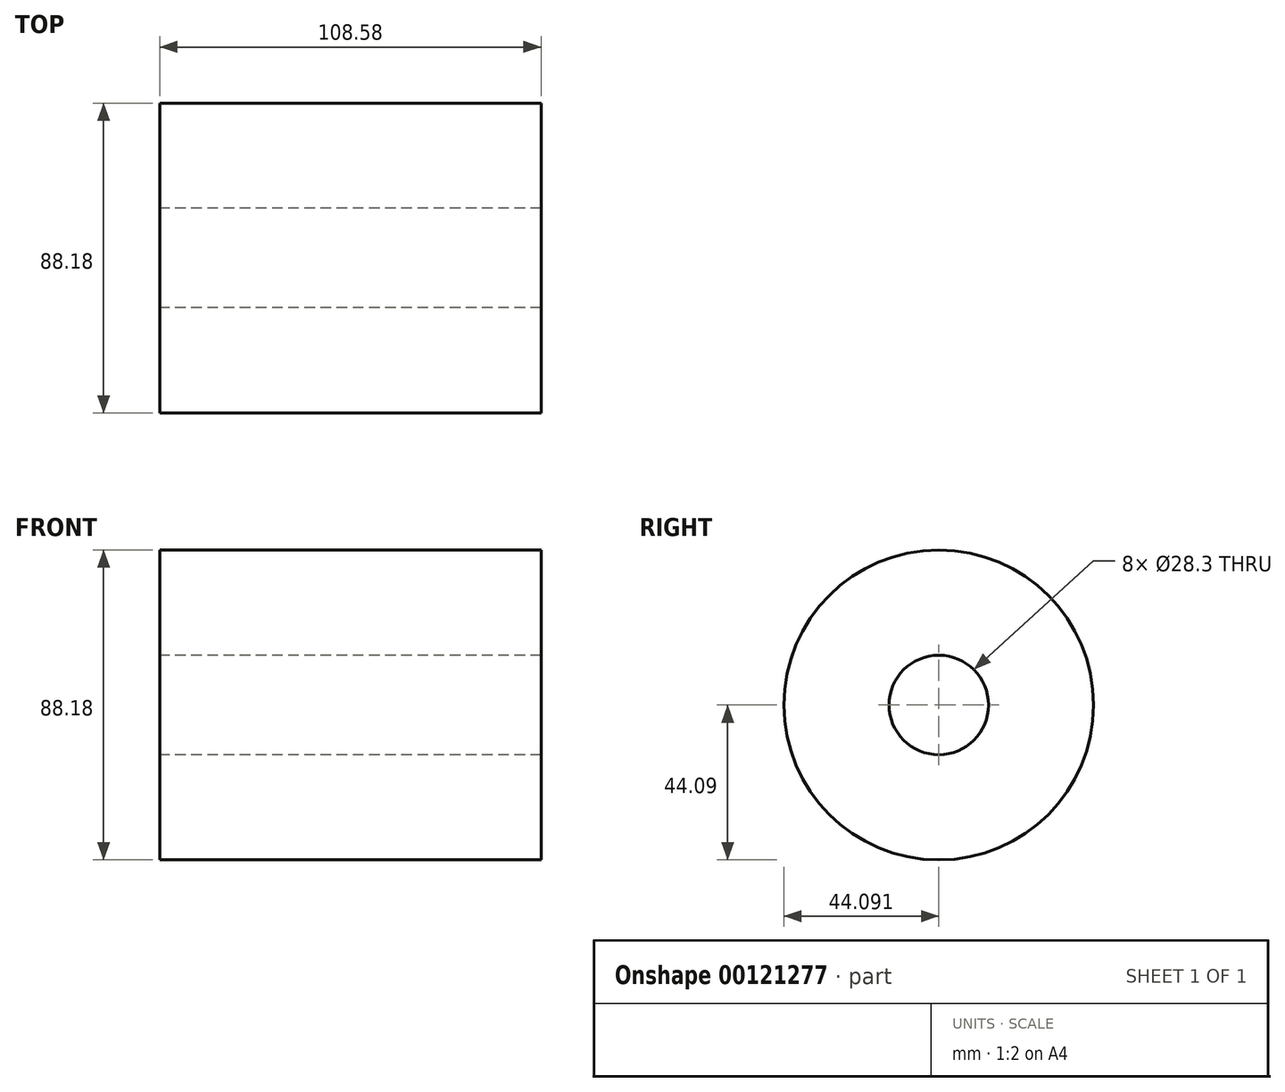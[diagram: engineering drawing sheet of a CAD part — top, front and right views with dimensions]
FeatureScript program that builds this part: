
annotation { "Feature Type Name" : "Feature", "Feature Type Description" : "" }
export const myFeature = defineFeature(function(context is Context, id is Id, definition is map)
    precondition{}
    {
        {
            var Q0;
            Q0=qCreatedBy(makeId("Top.planeOp"),FACE);
            var sketch = newSketch(context, id + "F0", { "sketchPlane" : qUnion([Q0])});
            skLineSegment(sketch, "E0", {"start": v(-59.06, 39.46) * mm, "end": v(66.68, 39.46) * mm});
            skLineSegment(sketch, "E1.bottom", {"start": v(-50.07, 25.3) * mm, "end": v(58.51, 25.3) * mm});
            skLineSegment(sketch, "E1.top", {"start": v(-50.07, -4.63) * mm, "end": v(58.51, -4.63) * mm});
            skLineSegment(sketch, "E1.left", {"start": v(-50.07, 25.3) * mm, "end": v(-50.07, -4.63) * mm});
            skLineSegment(sketch, "E1.right", {"start": v(58.51, 25.3) * mm, "end": v(58.51, -4.63) * mm});
            skSolve(sketch);
        }
        {
            var Q0;
            Q0=makeQuery(id+"F0.imprint","IMPRINT",FACE,{"disambiguationData":[TD([[makeQuery(id+"F0.imprint","IMPRINT",EDGE,{"derivedFrom":sQuery(id+"F0.wireOp",EDGE,"E1.bottom")}),-1.0]])]});
            var Q1;
            Q1=sQuery(id+"F0.wireOp",EDGE,"E0");
            revolve(context, id + "F1", {"entities" : qUnion([Q0]), "axis" : qUnion([Q1]), "revolveType" : RevolveType.FULL});
        }
    });
